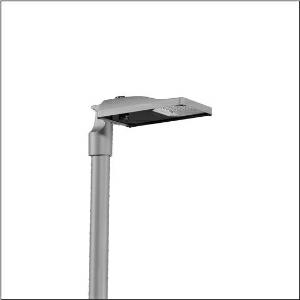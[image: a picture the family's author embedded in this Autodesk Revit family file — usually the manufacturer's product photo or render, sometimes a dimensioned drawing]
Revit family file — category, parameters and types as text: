
# Revit family: streetlight_sl_31_micro___st1_0a_5xh5d71t08da_8a50
name_source: partatom
category: Lighting Fixtures
units: mm (PartAtom-declared; Revit-internal decimal feet)

## family parameters
Cut with Voids When Loaded = No
Host = Face
Light Source = No
Part Type = Normal
Room Calculation Point = No
Round Connector Dimension = Use Diameter
Shared = No

## types (1)
- --- (1 x LED, 3990 lm, 37.7 W, 2200K)
    Apparent Load = 38 VA
    CIE Flux Codes = 37 72 97 100 100
    Color Rendering = 70
    Color Temperature = 2200K
    Default Elevation = 1800 mm
    Description = Streetlight SL 31 micro D4i, Desk-Remote mast luminaire for post-top, side-entry; light control with lens of PMMA; light distribution: ST1.0a, direct asymmetric distribution, for standard-compliant lighting for roads and squares; LED: luminous flux: 3.990lm, light colour: 722, colour temperature: 2200K; luminous efficacy: 105,8lm/W; control: pre-setting: logarithmic dimming characteristic, flexible luminous flux parameterisation, time-dependent luminous flux control, constant luminous flux control, power reduction, intelligent temperature release in ECG and LED module, overheat protection; luminaire housing, of diecast aluminium, SITECO metallic grey (DB 702S), corrosivity category C5 high according to DIN EN ISO 12944; cover of toughened safety glass, transparent, opened without tools; mast flange of diecast aluminium, SITECO metallic grey (DB 702S), spigot size: 76/60mm, mast flange included unmounted; cable length: 6,5m, connection cable pre-assembled; mains connection: 220..240V, AC, 50/60Hz; power consumption (at start of service life): 37,7W / (at end of service life): 40,9W / (with reduced operation 50%): 16,3W; protection rating (complete): IP66; insulation class (complete): insulation class II (safety insulation); impact resistance: IK09; certification: CE, ENEC, ENEC+, VDE, UKCA, ZD4i; permissible operating ambient temperature for outdoor applications: -40..+50°C; packaging unit: 1 piece

Light Distribution: ST1.0a
    Height = 76 mm
    Lamp = 1 x LED
    Lamp Light Flux = 3990 lm
    Lamp Power = 37.7 W
    Lamp count = 1
    Length = 467 mm
    Luminous efficacy = 106 lm/W
    Manufacturer = Siteco
    ModVariant = No
    Model = 5XH5D71T08DA
    Number of Poles = 1
    OnlyDefault = Yes
    Power Factor = 1
    Product Name = Streetlight SL 31 micro | ST1.0a
    Product group = mast luminaire | pylon top
    ProductGroupID = 6100
    Protection Class = Protection class II
    Protection Degree = IP 66
    RLX_Detail_Level = 1
    RLX_Emergency_Light_Flux = 0 lm
    RLX_Emergency_Type = 0
    RLX_Emergency_Type_DB = No
    RlxData = <blob elided: 23397 chars, md5=a0793097>
    Socket = socket
    Standby Power = 0 W
    System Light Flux = 3990 lm
    System Power = 38 W
    Type Comments = factory setting: luminous flux: 100 % | dim-lin: 254 | 745 mA
    Type Image = l_1300315.jpg
    URL = http://relux.com
    VarID = @adj_009321
    Voltage = 0 V
    Weight = 0.00 kg
    Width = 265 mm

## geometry (parser evidence)
native form markers: Blend x4, Sweep x10
no freeform markers — native parametric forms only
